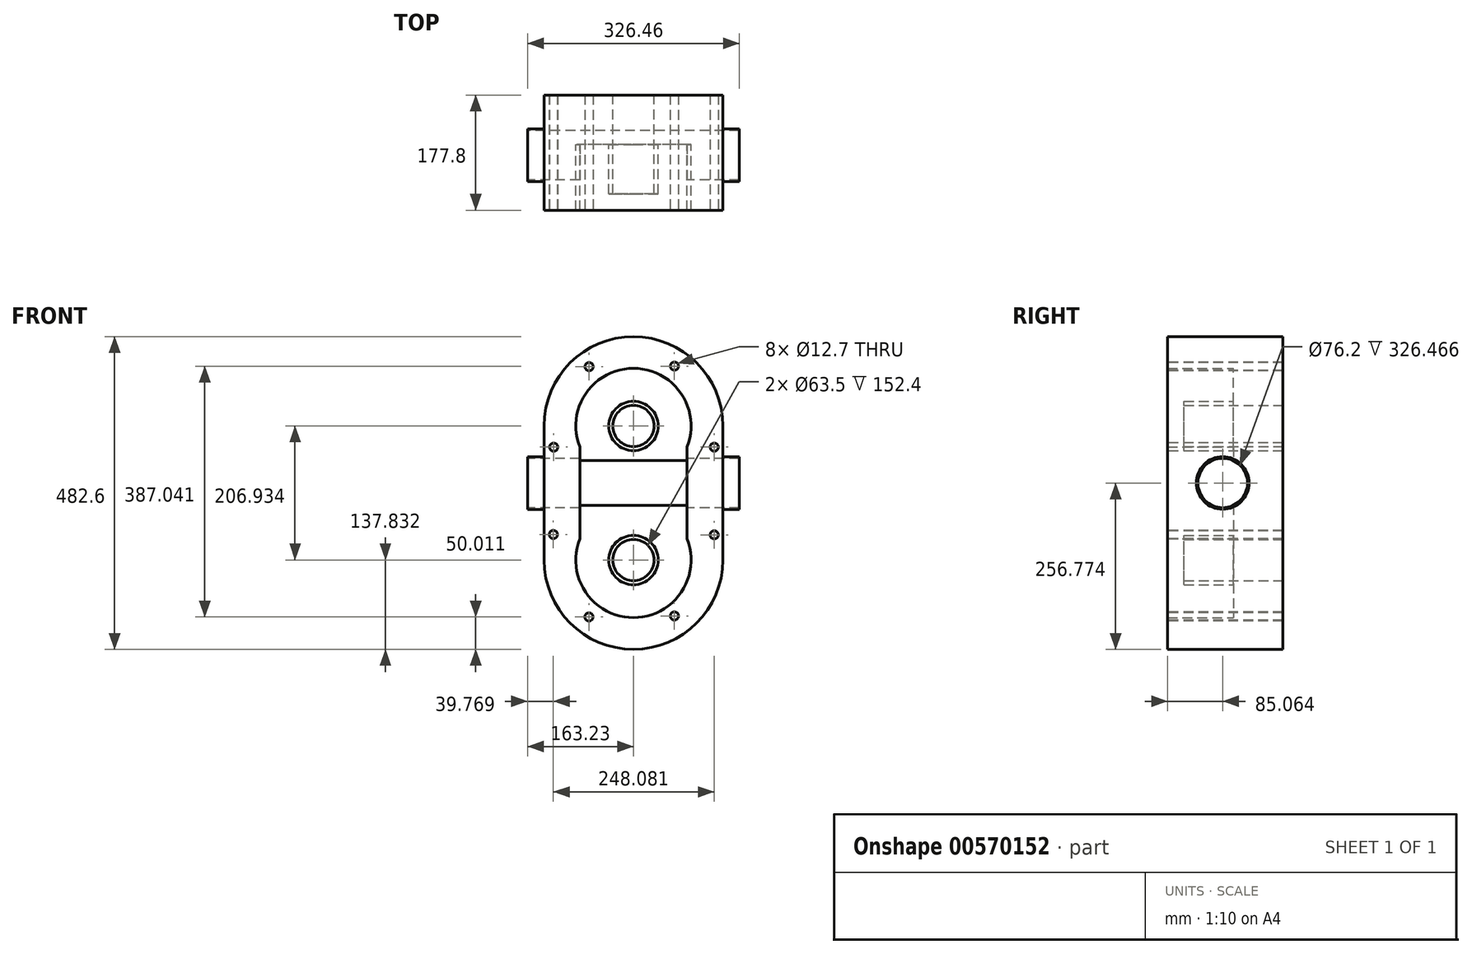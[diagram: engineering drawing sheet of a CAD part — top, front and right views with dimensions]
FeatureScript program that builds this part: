
annotation { "Feature Type Name" : "Feature", "Feature Type Description" : "" }
export const myFeature = defineFeature(function(context is Context, id is Id, definition is map)
    precondition{}
    {
        {
            var Q0;
            Q0=qCreatedBy(makeId("Front.planeOp"),FACE);
            var sketch = newSketch(context, id + "F0", { "sketchPlane" : qUnion([Q0])});
            skArc(sketch, "E0", {"start": v(137.83, 32.68) * mm, "mid": v(0, 170.5) * mm, "end": v(-137.83, 32.68) * mm});
            skArc(sketch, "E1", {"start": v(-137.83, -174.26) * mm, "mid": v(0, -312.1) * mm, "end": v(137.83, -174.26) * mm});
            skLineSegment(sketch, "E2", {"start": v(-137.83, 32.68) * mm, "end": v(-137.83, -174.26) * mm});
            skLineSegment(sketch, "E3", {"start": v(137.83, 32.68) * mm, "end": v(137.83, -174.26) * mm});
            skArc(sketch, "E4", {"start": v(82.68, 0) * mm, "mid": v(0, 121.58) * mm, "end": v(-82.68, 0) * mm});
            skArc(sketch, "E5", {"start": v(-82.68, -141.58) * mm, "mid": v(0, -263.16) * mm, "end": v(82.68, -141.58) * mm});
            skLineSegment(sketch, "E6", {"start": v(-82.68, 0) * mm, "end": v(-82.68, -141.58) * mm});
            skLineSegment(sketch, "E7", {"start": v(82.68, 0) * mm, "end": v(82.68, -141.58) * mm});
            skCircle(sketch, "E8", {"center": v(0, 32.68) * mm, "radius": 38.1 * mm});
            skCircle(sketch, "E9", {"center": v(0, -174.26) * mm, "radius": 38.1 * mm});
            skCircle(sketch, "E10", {"center": v(0, -174.26) * mm, "radius": 31.75 * mm});
            skCircle(sketch, "E11", {"center": v(0, 32.68) * mm, "radius": 31.75 * mm});
            skSolve(sketch);
        }
        {
            var Q0;
            Q0=makeQuery(id+"F0.imprint","IMPRINT",FACE,{"disambiguationData":[TD([[makeQuery(id+"F0.imprint","IMPRINT",EDGE,{"derivedFrom":sQuery(id+"F0.wireOp",EDGE,"E0")}),1.0]])]});
            extrude(context, id + "F1", {"entities" : qUnion([Q0]), "depth" : 177.8 * mm, "offsetDistance" : 25.4 * mm});
        }
        {
            var Q0;
            Q0=makeQuery(id+"F0.imprint","IMPRINT",FACE,{"disambiguationData":[TD([[makeQuery(id+"F0.imprint","IMPRINT",EDGE,{"derivedFrom":sQuery(id+"F0.wireOp",EDGE,"E4")}),1.0]])]});
            extrude(context, id + "F2", {"entities" : qUnion([Q0]), "operationType" : NewBodyOperationType.ADD, "depth" : 76.2 * mm, "offsetDistance" : 25.4 * mm});
        }
        {
            var Q0;
            Q0=makeQuery(id+"F0.imprint","IMPRINT",FACE,{"disambiguationData":[TD([[makeQuery(id+"F0.imprint","IMPRINT",EDGE,{"derivedFrom":sQuery(id+"F0.wireOp",EDGE,"E9")}),1.0]])]});
            var Q1;
            Q1=makeQuery(id+"F0.imprint","IMPRINT",FACE,{"disambiguationData":[TD([[makeQuery(id+"F0.imprint","IMPRINT",EDGE,{"derivedFrom":sQuery(id+"F0.wireOp",EDGE,"E8")}),1.0]])]});
            extrude(context, id + "F3", {"entities" : qUnion([Q0, Q1]), "operationType" : NewBodyOperationType.ADD, "depth" : 152.4 * mm, "offsetDistance" : 25.4 * mm});
        }
        {
            var Q0;
            Q0=makeQuery(id+"F1.opExtrude","SWEPT_FACE",FACE,{"disambiguationData":[OSD([sQuery(id+"F0.wireOp",EDGE,"E2")])]});
            var sketch = newSketch(context, id + "F4", { "sketchPlane" : qUnion([Q0])});
            skCircle(sketch, "E12", {"center": v(92.74, -55.32) * mm, "radius": 38.1 * mm});
            skCircle(sketch, "E13", {"center": v(92.74, -55.32) * mm, "radius": 40.64 * mm});
            skSolve(sketch);
        }
        {
            var Q0;
            Q0=sQuery(id+"F4.wireOp",VERTEX,"E12.center");
            var Q1;
            Q1=makeQuery(id+"F1.opExtrude","SWEPT_BODY",BODY,{"disambiguationData":[OSD([sQuery(id+"F0.wireOp",EDGE,"E0"),sQuery(id+"F0.wireOp",EDGE,"E1"),sQuery(id+"F0.wireOp",EDGE,"E2"),sQuery(id+"F0.wireOp",EDGE,"E3"),sQuery(id+"F0.wireOp",EDGE,"E4"),sQuery(id+"F0.wireOp",EDGE,"E5"),sQuery(id+"F0.wireOp",EDGE,"E6"),sQuery(id+"F0.wireOp",EDGE,"E7")])]});
            hole(context, id + "F5", {"style" : HoleStyle.SIMPLE, "endStyle" : HoleEndStyle.THROUGH, "holeDiameter" : 76.2 * mm, "isTappedThrough" : true, "tappedDepth" : 12.7 * mm, "tapClearance" : 3, "locations" : qUnion([Q0]), "scope" : qUnion([Q1])});
        }
        {
            var Q0;
            Q0=makeQuery(id+"F4.imprint","IMPRINT",FACE,{"disambiguationData":[TD([[makeQuery(id+"F4.imprint","IMPRINT",EDGE,{"derivedFrom":sQuery(id+"F4.wireOp",EDGE,"E12")}),-1.0]])]});
            extrude(context, id + "F6", {"entities" : qUnion([Q0]), "operationType" : NewBodyOperationType.ADD, "depth" : 25.4 * mm, "offsetDistance" : 25.4 * mm});
        }
        {
            var Q0;
            Q0=makeQuery(id+"F1.opExtrude","SWEPT_FACE",FACE,{"disambiguationData":[OSD([sQuery(id+"F0.wireOp",EDGE,"E3")])]});
            var sketch = newSketch(context, id + "F7", { "sketchPlane" : qUnion([Q0])});
            skCircle(sketch, "E14", {"center": v(-92.74, -55.32) * mm, "radius": 40.64 * mm});
            skCircle(sketch, "E15", {"center": v(-92.74, -55.32) * mm, "radius": 38.1 * mm});
            skSolve(sketch);
        }
        {
            var Q0;
            Q0=makeQuery(id+"F7.imprint","IMPRINT",FACE,{"disambiguationData":[TD([[makeQuery(id+"F7.imprint","IMPRINT",EDGE,{"derivedFrom":sQuery(id+"F7.wireOp",EDGE,"E14")}),1.0]])]});
            extrude(context, id + "F8", {"entities" : qUnion([Q0]), "operationType" : NewBodyOperationType.ADD, "depth" : 25.4 * mm, "offsetDistance" : 25.4 * mm});
        }
        {
            var Q0;
            Q0=makeQuery(id+"F1.opExtrude","CAP_FACE",FACE,{"disambiguationData":[OSD([sQuery(id+"F0.wireOp",EDGE,"E0"),sQuery(id+"F0.wireOp",EDGE,"E1"),sQuery(id+"F0.wireOp",EDGE,"E2"),sQuery(id+"F0.wireOp",EDGE,"E3"),sQuery(id+"F0.wireOp",EDGE,"E4"),sQuery(id+"F0.wireOp",EDGE,"E5"),sQuery(id+"F0.wireOp",EDGE,"E6"),sQuery(id+"F0.wireOp",EDGE,"E7")])],"isStart":false});
            var sketch = newSketch(context, id + "F9", { "sketchPlane" : qUnion([Q0])});
            skPoint(sketch, "E16.centerSnap0", {"position": v(0, 121.58) * mm});
            skPoint(sketch, "E17.centerSnap0", {"position": v(0, -263.16) * mm});
            skCircle(sketch, "E18", {"center": v(-68.3, 124.21) * mm, "radius": 6.93 * mm});
            skCircle(sketch, "E19", {"center": v(63.23, 124.96) * mm, "radius": 7.54 * mm});
            skCircle(sketch, "E20", {"center": v(124.62, 0) * mm, "radius": 8.07 * mm});
            skCircle(sketch, "E21", {"center": v(124.62, -135.4) * mm, "radius": 7.58 * mm});
            skCircle(sketch, "E22", {"center": v(-122.92, 0) * mm, "radius": 8.01 * mm});
            skCircle(sketch, "E23", {"center": v(-123.46, -134.86) * mm, "radius": 8.14 * mm});
            skCircle(sketch, "E24", {"center": v(-68.58, -262.08) * mm, "radius": 7.58 * mm});
            skCircle(sketch, "E25", {"center": v(63.17, -260.55) * mm, "radius": 8 * mm});
            skSolve(sketch);
        }
        {
            var Q0;
            Q0=sQuery(id+"F9.wireOp",VERTEX,"E18.center");
            var Q1;
            Q1=sQuery(id+"F9.wireOp",VERTEX,"E19.center");
            var Q2;
            Q2=sQuery(id+"F9.wireOp",VERTEX,"E20.center");
            var Q3;
            Q3=sQuery(id+"F9.wireOp",VERTEX,"E21.center");
            var Q4;
            Q4=sQuery(id+"F9.wireOp",VERTEX,"E25.center");
            var Q5;
            Q5=sQuery(id+"F9.wireOp",VERTEX,"E24.center");
            var Q6;
            Q6=sQuery(id+"F9.wireOp",VERTEX,"E23.center");
            var Q7;
            Q7=sQuery(id+"F9.wireOp",VERTEX,"E22.center");
            var Q8;
            Q8=makeQuery(id+"F1.opExtrude","SWEPT_BODY",BODY,{"disambiguationData":[OSD([sQuery(id+"F0.wireOp",EDGE,"E0"),sQuery(id+"F0.wireOp",EDGE,"E1"),sQuery(id+"F0.wireOp",EDGE,"E2"),sQuery(id+"F0.wireOp",EDGE,"E3"),sQuery(id+"F0.wireOp",EDGE,"E4"),sQuery(id+"F0.wireOp",EDGE,"E5"),sQuery(id+"F0.wireOp",EDGE,"E6"),sQuery(id+"F0.wireOp",EDGE,"E7")])]});
            hole(context, id + "F10", {"style" : HoleStyle.SIMPLE, "endStyle" : HoleEndStyle.THROUGH, "holeDiameter" : 12.7 * mm, "isTappedThrough" : true, "tappedDepth" : 12.7 * mm, "tapClearance" : 3, "locations" : qUnion([Q0, Q1, Q2, Q3, Q4, Q5, Q6, Q7]), "scope" : qUnion([Q8]), "majorDiameter" : 6.35 * mm});
        }
    });
